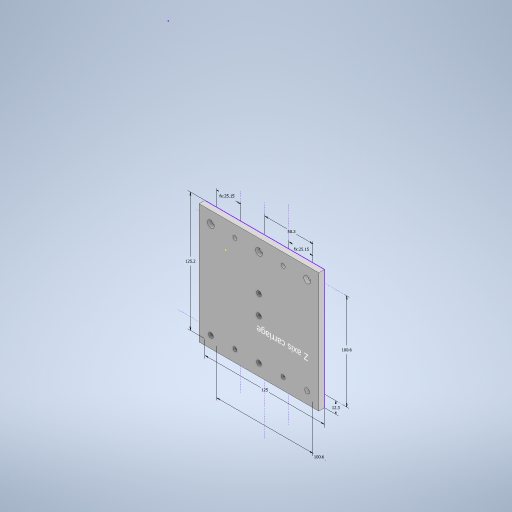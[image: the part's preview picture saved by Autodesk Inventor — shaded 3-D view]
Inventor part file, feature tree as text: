
AUTODESK INVENTOR PART (.ipt)
format: ipt  version: 2023.2 (Build 272271000, 271)  size: 455,168 bytes
history: native  units: mm
features: sketch x4, hole x4, reference x3, other x3, extrude x1
ambient origin geometry x8: Origin, YZ Plane, XZ Plane, XY Plane, X Axis, Y Axis, Z Axis, Center Point
bodies: Solid1 (feature_tree)
feature tree (15):
  sketch  "Sketch1"  dims[d0=125.0mm d1=125.2mm d6=100.6mm d11=6.0mm d12=0.0mm d48=12.3mm]
  extrude  "Extrusion1"  Depth=6.0mm
  hole  "Hole6"  [1 undecoded]
  sketch  "Sketch2"  dims[d49=100.6mm d50=50.3mm]
  sketch  "Sketch3"  dims[d51=5.1mm d52=6.0mm d53=9.2mm d54=2.0mm d55=90.0deg d56=8.0mm d57=20.594885mm]
  hole  "Hole7"  [1 undecoded]
  hole  "Hole8"  [1 undecoded]
  hole  "Hole9"  [1 undecoded]
  reference  "Reference7"
  sketch  "Sketch5"  dims[d58=7.2mm d59=6.0mm d60=12.25mm d61=2.0mm d62=90.0deg d63=8.0mm d64=20.594885mm d65=5.1mm d66=6.0mm d67=9.2mm d68=2.0mm d69=90.0deg d70=8.0mm d71=20.594885mm d72=25.15mm d73=25.15mm d74=4.2mm d75=6.0mm d76=9.2mm d77=2.0mm d78=90.0deg d79=8.0mm d80=20.594885mm]
  reference  "Reference8"
  reference  "Reference9"
  parser-record x1  (decoder bookkeeping rows leaked as tree rows — omitted from the tree; the rows remain in map.json)
  other  "Main Assembly.iam"
  other  "Z axis carriage small 2:1"
note: 4 required parameter values undecoded (feature->parameter linkage not recoverable at this tier; creation-order binding heuristic only, values carry confidence <= 0.55)
note: 1 file-system path scrubbed to <path> (originals preserved in map.json)
